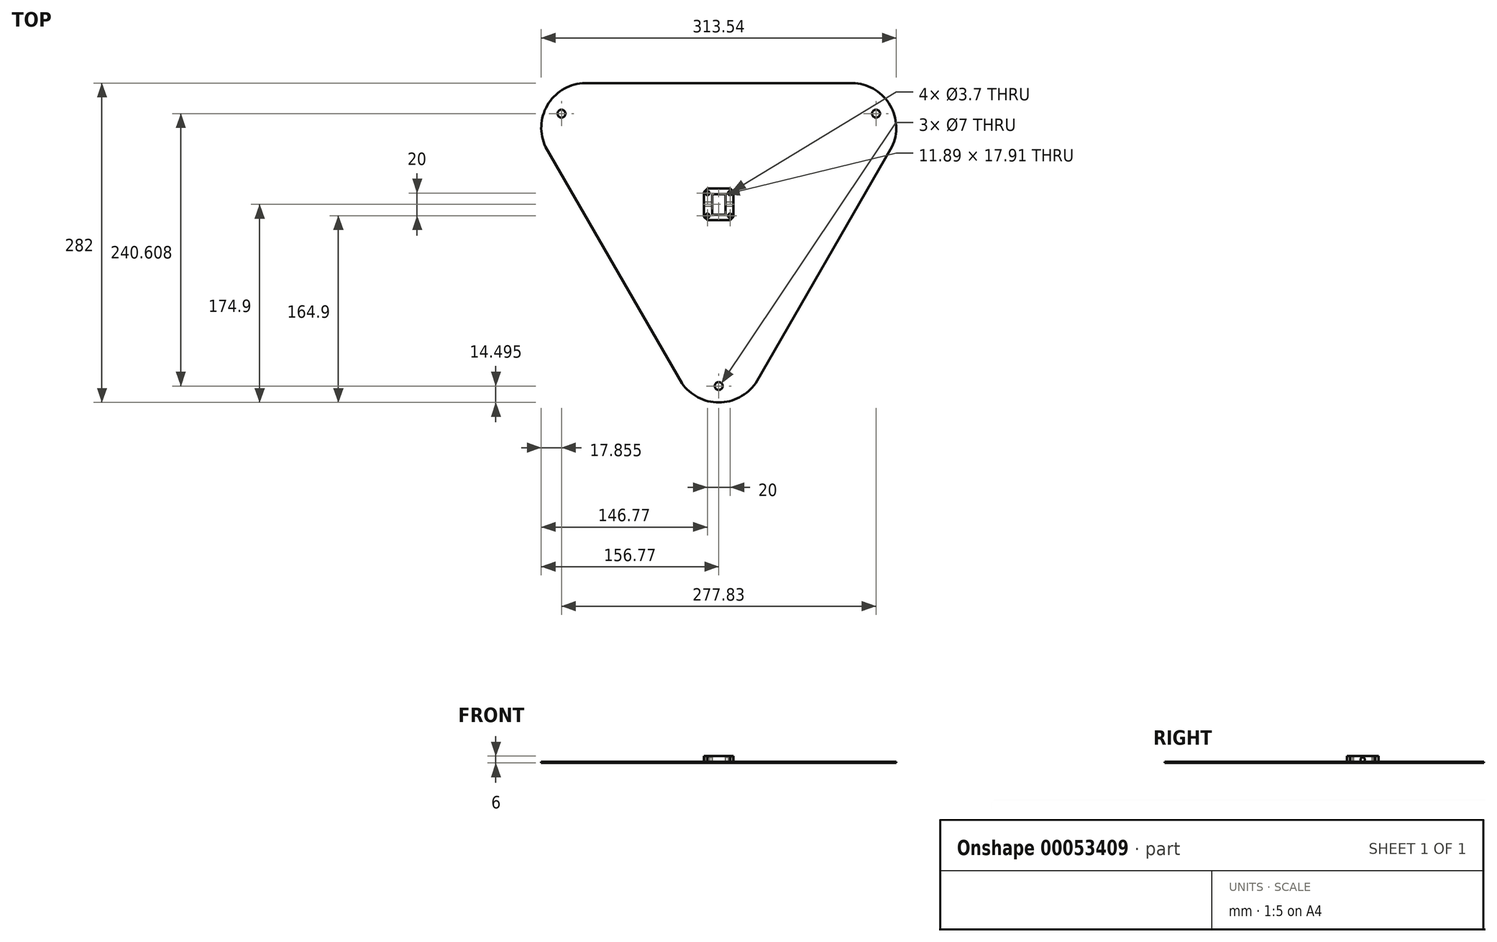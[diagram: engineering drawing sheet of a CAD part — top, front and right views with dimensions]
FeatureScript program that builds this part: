
annotation { "Feature Type Name" : "Feature", "Feature Type Description" : "" }
export const myFeature = defineFeature(function(context is Context, id is Id, definition is map)
    precondition{}
    {
        {
            var Q0;
            Q0=qCreatedBy(makeId("Top.planeOp"),FACE);
            var sketch = newSketch(context, id + "F0", { "sketchPlane" : qUnion([Q0])});
            skCircle(sketch, "E0.cCircle", {"center": v(0, 0) * mm, "radius": 107.1 * mm, "construction": true});
            skLineSegment(sketch, "E0.0", {"start": v(-120.5, 107.1) * mm, "end": v(120.5, 107.1) * mm});
            skLineSegment(sketch, "E0.1", {"start": v(153, 50.8) * mm, "end": v(32.5, -157.9) * mm});
            skLineSegment(sketch, "E0.2", {"start": v(-32.5, -157.9) * mm, "end": v(-153, 50.8) * mm});
            skPoint(sketch, "E0.0.midPoint", {"position": v(0, 107.1) * mm});
            skLineSegment(sketch, "E1", {"start": v(-153, 50.8) * mm, "end": v(-120.5, 107.1) * mm, "construction": true});
            skLineSegment(sketch, "E2.1.0", {"start": v(32.5, -157.9) * mm, "end": v(-32.5, -157.9) * mm, "construction": true});
            skLineSegment(sketch, "E2.2.0", {"start": v(120.5, 107.1) * mm, "end": v(153, 50.8) * mm, "construction": true});
            skArc(sketch, "E3", {"start": v(-120.5, 107.1) * mm, "mid": v(-151.47, 87.45) * mm, "end": v(-153, 50.8) * mm});
            skArc(sketch, "E4.1.0", {"start": v(-32.5, -157.9) * mm, "mid": v(0, -174.9) * mm, "end": v(32.5, -157.9) * mm});
            skArc(sketch, "E4.2.0", {"start": v(153, 50.8) * mm, "mid": v(151.47, 87.45) * mm, "end": v(120.5, 107.1) * mm});
            skCircle(sketch, "E5", {"center": v(0, -160.4) * mm, "radius": 3.5 * mm});
            skPoint(sketch, "E5.centerSnap0", {"position": v(0, -157.9) * mm});
            skCircle(sketch, "E6.1.0", {"center": v(138.92, 80.2) * mm, "radius": 3.5 * mm});
            skCircle(sketch, "E6.2.0", {"center": v(-138.92, 80.2) * mm, "radius": 3.5 * mm});
            skPoint(sketch, "E7.orphan", {"position": v(-185.5, 107.1) * mm});
            skPoint(sketch, "E8.orphan", {"position": v(185.5, 107.1) * mm});
            skPoint(sketch, "E9.orphan", {"position": v(0, -214.2) * mm});
            skSolve(sketch);
        }
        {
            var Q0;
            {var subQ0=sQuery(id+"F0.wireOp",EDGE,"E3");Q0=makeQuery(id+"F0.imprint","IMPRINT",FACE,{"disambiguationData":[TD([[makeQuery(id+"F0.imprint","IMPRINT",EDGE,{"derivedFrom":subQ0}),1.0]])]});}
            extrude(context, id + "F1", {"entities" : qUnion([Q0]), "depth" : 1 * mm});
        }
        {
            var Q0;
            Q0=qCreatedBy(makeId("Top.planeOp"),FACE);
            var sketch = newSketch(context, id + "F2", { "sketchPlane" : qUnion([Q0])});
            skCircle(sketch, "E10", {"center": v(-10, 10) * mm, "radius": 1.85 * mm});
            skCircle(sketch, "E11.1.0", {"center": v(-10, -10) * mm, "radius": 1.85 * mm});
            skCircle(sketch, "E11.2.0", {"center": v(10, -10) * mm, "radius": 1.85 * mm});
            skCircle(sketch, "E11.3.0", {"center": v(10, 10) * mm, "radius": 1.85 * mm});
            skPoint(sketch, "E11.center", {"position": v(0, 0) * mm});
            skLineSegment(sketch, "E12.bottom", {"start": v(13, 14) * mm, "end": v(-13, 14) * mm});
            skLineSegment(sketch, "E12.top", {"start": v(13, -14) * mm, "end": v(-13, -14) * mm});
            skLineSegment(sketch, "E12.left", {"start": v(13, 14) * mm, "end": v(13, -14) * mm});
            skLineSegment(sketch, "E12.right", {"start": v(-13, 14) * mm, "end": v(-13, -14) * mm});
            skLineSegment(sketch, "E13.bottom", {"start": v(-5.95, 8.96) * mm, "end": v(5.95, 8.96) * mm});
            skLineSegment(sketch, "E13.top", {"start": v(-5.95, -8.96) * mm, "end": v(5.95, -8.96) * mm});
            skLineSegment(sketch, "E13.left", {"start": v(-5.95, 8.96) * mm, "end": v(-5.95, -8.96) * mm});
            skLineSegment(sketch, "E13.right", {"start": v(5.95, 8.96) * mm, "end": v(5.95, -8.96) * mm});
            skSolve(sketch);
        }
        {
            var Q0;
            Q0=makeQuery(id+"F2.imprint","IMPRINT",FACE,{"disambiguationData":[TD([[makeQuery(id+"F2.imprint","IMPRINT",EDGE,{"derivedFrom":sQuery(id+"F2.wireOp",EDGE,"E10")}),-1.0]])]});
            extrude(context, id + "F3", {"entities" : qUnion([Q0]), "depth" : 6 * mm});
        }
        {
            var Q0;
            Q0=makeQuery(id+"F3.opExtrude","SWEPT_FACE",FACE,{"disambiguationData":[OSD([sQuery(id+"F2.wireOp",EDGE,"E12.right")])]});
            var sketch = newSketch(context, id + "F4", { "sketchPlane" : qUnion([Q0])});
            skCircle(sketch, "E14", {"center": v(0, 3) * mm, "radius": 1.95 * mm});
            skPoint(sketch, "E14.centerSnap0", {"position": v(-14, 3) * mm});
            skPoint(sketch, "E14.centerSnap1", {"position": v(0, 0) * mm});
            skSolve(sketch);
        }
        {
            var Q0;
            Q0=sQuery(id+"F4.wireOp",VERTEX,"E14.center");
            var Q1;
            Q1=makeQuery(id+"F3.opExtrude","SWEPT_BODY",BODY,{"disambiguationData":[OSD([sQuery(id+"F2.wireOp",EDGE,"E10"),sQuery(id+"F2.wireOp",EDGE,"E11.1.0"),sQuery(id+"F2.wireOp",EDGE,"E11.2.0"),sQuery(id+"F2.wireOp",EDGE,"E11.3.0"),sQuery(id+"F2.wireOp",EDGE,"E12.bottom"),sQuery(id+"F2.wireOp",EDGE,"E12.top"),sQuery(id+"F2.wireOp",EDGE,"E12.left"),sQuery(id+"F2.wireOp",EDGE,"E12.right"),sQuery(id+"F2.wireOp",EDGE,"E13.bottom"),sQuery(id+"F2.wireOp",EDGE,"E13.top"),sQuery(id+"F2.wireOp",EDGE,"E13.left"),sQuery(id+"F2.wireOp",EDGE,"E13.right")])]});
            hole(context, id + "F5", {"style" : HoleStyle.SIMPLE, "endStyle" : HoleEndStyle.BLIND, "holeDiameter" : 3.9 * mm, "holeDepth" : 45 * mm, "locations" : qUnion([Q0]), "scope" : qUnion([Q1])});
        }
        {
            var Q0;
            Q0=makeQuery(id+"F3.opExtrude","SWEPT_EDGE",EDGE,{"disambiguationData":[OSD([sQuery(id+"F2.wireOp",EDGE,"E12.bottom"),sQuery(id+"F2.wireOp",EDGE,"E12.right")])]});
            var Q1;
            Q1=makeQuery(id+"F3.opExtrude","SWEPT_EDGE",EDGE,{"disambiguationData":[OSD([sQuery(id+"F2.wireOp",EDGE,"E12.bottom"),sQuery(id+"F2.wireOp",EDGE,"E12.left")])]});
            var Q2;
            Q2=makeQuery(id+"F3.opExtrude","SWEPT_EDGE",EDGE,{"disambiguationData":[OSD([sQuery(id+"F2.wireOp",EDGE,"E12.top"),sQuery(id+"F2.wireOp",EDGE,"E12.right")])]});
            var Q3;
            Q3=makeQuery(id+"F3.opExtrude","SWEPT_EDGE",EDGE,{"disambiguationData":[OSD([sQuery(id+"F2.wireOp",EDGE,"E12.top"),sQuery(id+"F2.wireOp",EDGE,"E12.left")])]});
            chamfer(context, id + "F6", {"entities" : qUnion([Q0, Q1, Q2, Q3]), "width" : 3 * mm, "tangentPropagation" : true});
        }
    });
